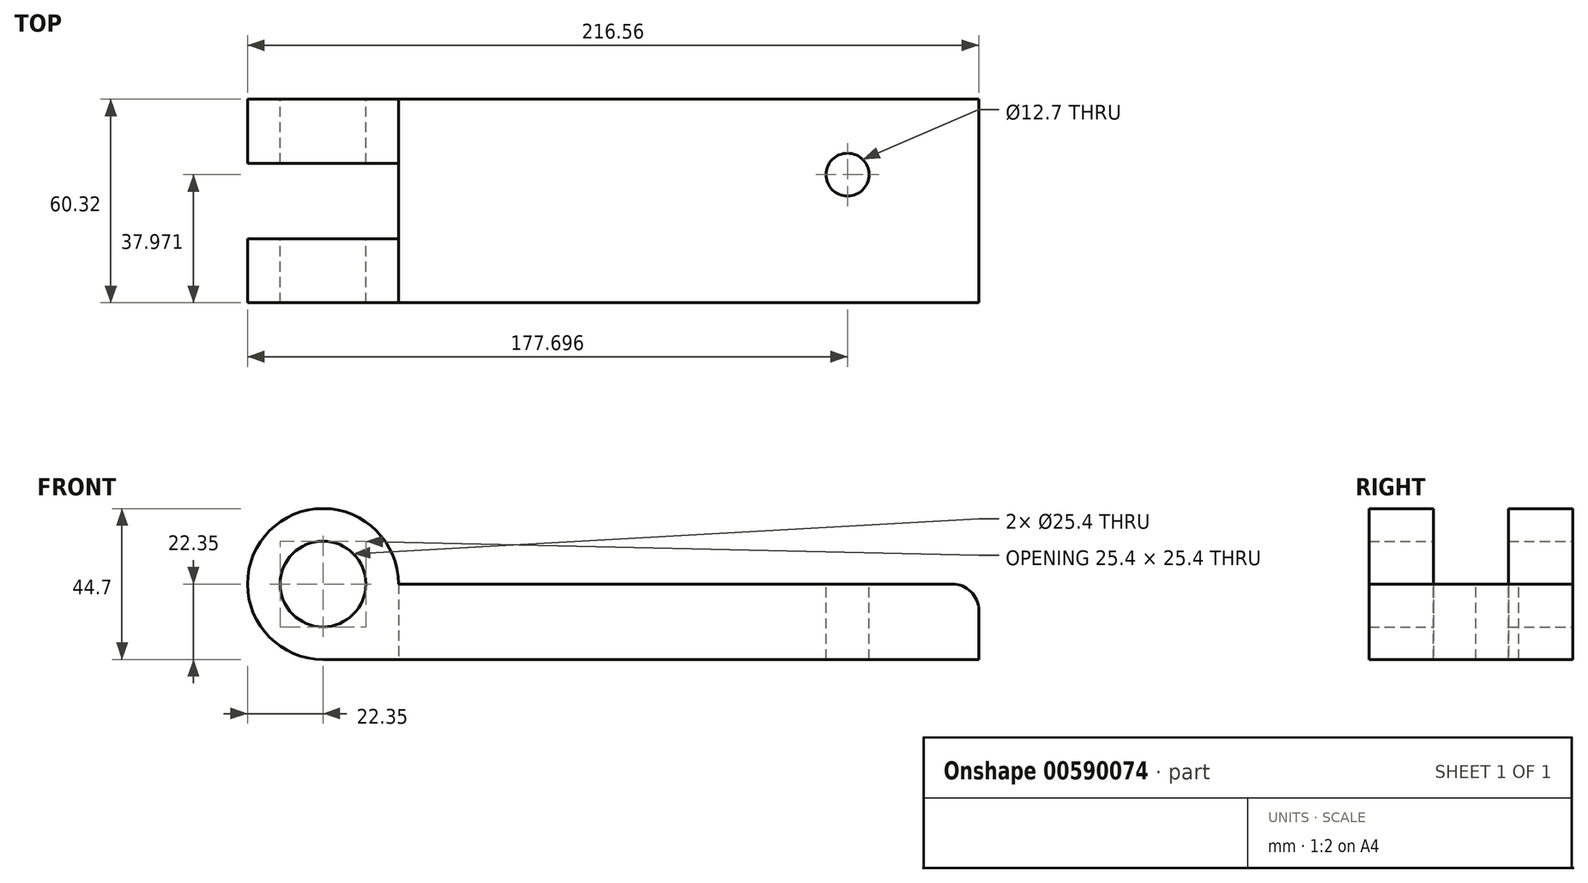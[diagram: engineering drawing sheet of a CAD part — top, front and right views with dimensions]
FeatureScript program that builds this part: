
annotation { "Feature Type Name" : "Feature", "Feature Type Description" : "" }
export const myFeature = defineFeature(function(context is Context, id is Id, definition is map)
    precondition{}
    {
        {
            var Q0;
            Q0=qCreatedBy(makeId("Front.planeOp"),FACE);
            var sketch = newSketch(context, id + "F0", { "sketchPlane" : qUnion([Q0])});
            skCircle(sketch, "E0", {"center": v(0, 0) * mm, "radius": 12.7 * mm});
            skCircle(sketch, "E1", {"center": v(0, 0) * mm, "radius": 22.35 * mm});
            skLineSegment(sketch, "E2.bottom", {"start": v(0, -22.35) * mm, "end": v(194.2, -22.35) * mm});
            skLineSegment(sketch, "E2.top", {"start": v(0, 0) * mm, "end": v(12.7, 0) * mm});
            skLineSegment(sketch, "E2.left", {"start": v(0, -22.35) * mm, "end": v(0, 0) * mm});
            skLineSegment(sketch, "E2.right", {"start": v(194.2, -22.35) * mm, "end": v(194.2, -7.87) * mm});
            skPoint(sketch, "E3.visualSharp", {"position": v(194.2, 0) * mm});
            skArc(sketch, "E3.filletArc", {"start": v(194.2, -7.87) * mm, "mid": v(191.9, -2.3) * mm, "end": v(186.33, 0) * mm});
            skLineSegment(sketch, "E4.trimOffspring", {"start": v(22.35, 0) * mm, "end": v(186.33, 0) * mm});
            skSolve(sketch);
        }
        {
            var Q0;
            {var subQ0=sQuery(id+"F0.wireOp",EDGE,"E2.bottom");Q0=makeQuery(id+"F0.imprint","IMPRINT",FACE,{"disambiguationData":[TD([[makeQuery(id+"F0.imprint","IMPRINT",EDGE,{"derivedFrom":subQ0}),1.0]])]});}
            extrude(context, id + "F1", {"entities" : qUnion([Q0]), "depth" : 60.32 * mm, "offsetDistance" : 25.4 * mm, "symmetric" : true});
        }
        {
            var Q0;
            {var subQ0=sQuery(id+"F0.wireOp",EDGE,"E0");var subQ1=makeQuery(id+"F0.imprint","INTERSECT",VERTEX,{"derivedFrom":[subQ0,sQuery(id+"F0.wireOp",EDGE,"E2.top")]});Q0=makeQuery(id+"F0.imprint","IMPRINT",FACE,{"disambiguationData":[TD([[makeQuery(id+"F0.imprint","IMPRINT",EDGE,{"disambiguationData":[TD([[subQ1,-1.0]])],"derivedFrom":subQ0}),-1.0]])]});}
            extrude(context, id + "F2", {"entities" : qUnion([Q0]), "operationType" : NewBodyOperationType.ADD, "depth" : 60.32 * mm, "offsetDistance" : 25.4 * mm, "symmetric" : true});
        }
        {
            var Q0;
            Q0=qCreatedBy(makeId("Top.planeOp"),FACE);
            var sketch = newSketch(context, id + "F3", { "sketchPlane" : qUnion([Q0])});
            skLineSegment(sketch, "E5.bottom", {"start": v(-22.35, -11.16) * mm, "end": v(22.35, -11.16) * mm});
            skLineSegment(sketch, "E5.top", {"start": v(-22.35, 11.16) * mm, "end": v(22.35, 11.16) * mm});
            skLineSegment(sketch, "E5.left", {"start": v(-22.35, -11.16) * mm, "end": v(-22.35, 11.16) * mm});
            skLineSegment(sketch, "E5.right", {"start": v(22.35, -11.16) * mm, "end": v(22.35, 11.16) * mm});
            skPoint(sketch, "E5.middle", {"position": v(0, 0) * mm});
            skSolve(sketch);
        }
        {
            var Q0;
            Q0=qSketchRegion(id+"F3",true);
            extrude(context, id + "F4", {"entities" : qUnion([Q0]), "operationType" : NewBodyOperationType.REMOVE, "depth" : 60.32 * mm, "offsetDistance" : 25.4 * mm, "symmetric" : true});
        }
        {
            var Q0;
            Q0=makeQuery(id+"F1.opExtrude","SWEPT_FACE",FACE,{"disambiguationData":[OSD([sQuery(id+"F0.wireOp",EDGE,"E4.trimOffspring")])]});
            var sketch = newSketch(context, id + "F5", { "sketchPlane" : qUnion([Q0])});
            skCircle(sketch, "E6", {"center": v(155.35, 7.81) * mm, "radius": 6.35 * mm});
            skSolve(sketch);
        }
        {
            var Q0;
            Q0=makeQuery(id+"F5.imprint","IMPRINT",FACE,{"disambiguationData":[TD([[makeQuery(id+"F5.imprint","IMPRINT",EDGE,{"derivedFrom":sQuery(id+"F5.wireOp",EDGE,"E6")}),1.0]])]});
            extrude(context, id + "F6", {"entities" : qUnion([Q0]), "operationType" : NewBodyOperationType.REMOVE, "oppositeDirection" : true, "depth" : 22.35 * mm, "offsetDistance" : 25.4 * mm});
        }
    });
